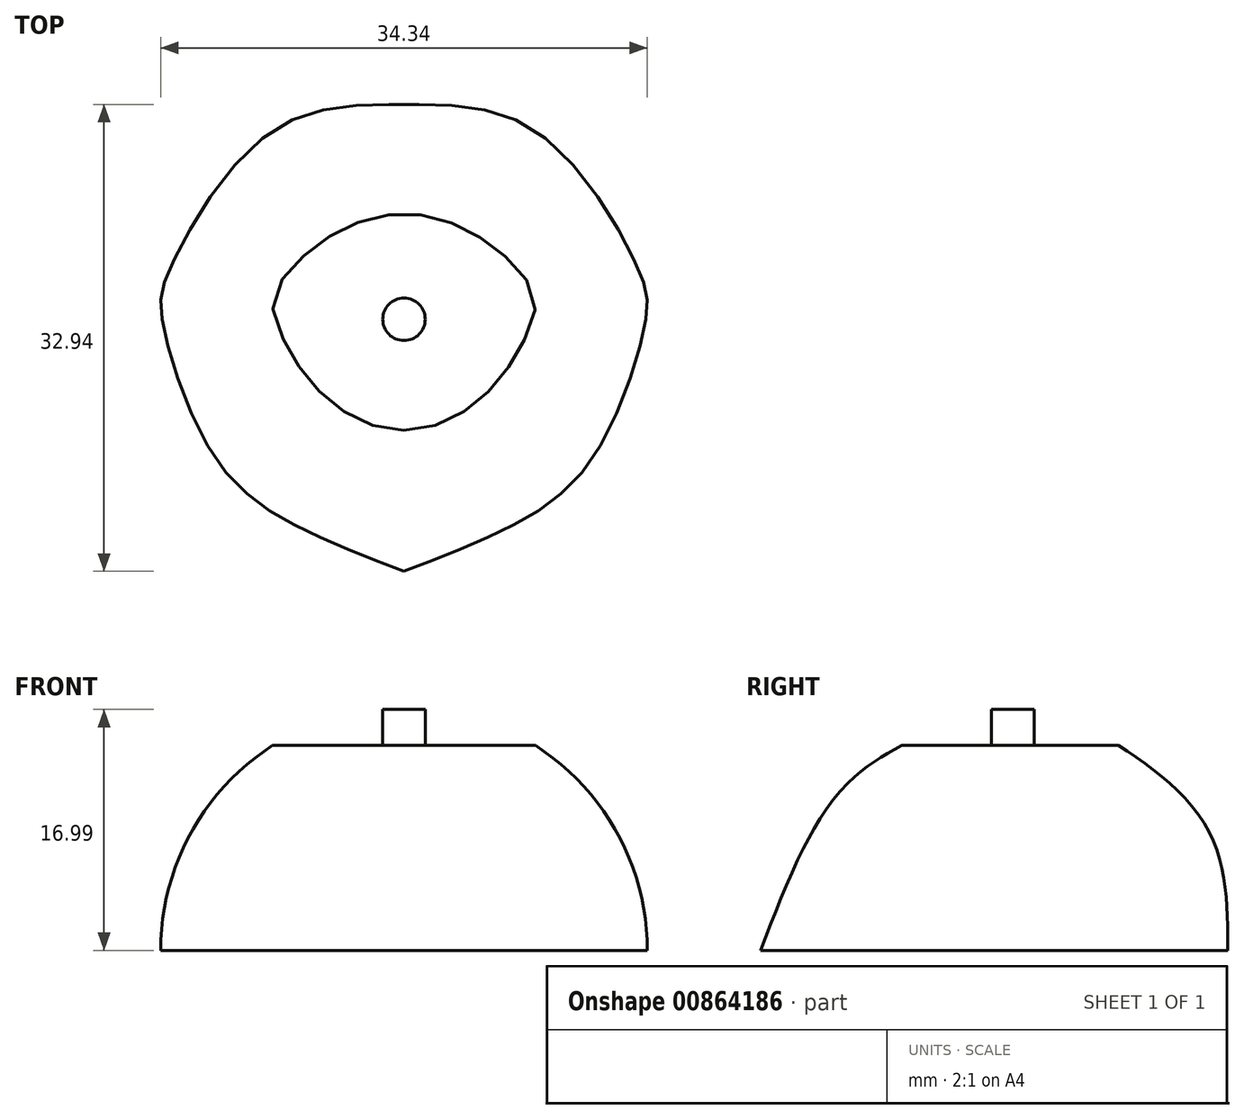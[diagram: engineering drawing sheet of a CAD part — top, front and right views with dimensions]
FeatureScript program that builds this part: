
annotation { "Feature Type Name" : "Feature", "Feature Type Description" : "" }
export const myFeature = defineFeature(function(context is Context, id is Id, definition is map)
    precondition{}
    {
        {
            var Q0;
            Q0=qCreatedBy(makeId("Top.planeOp"),FACE);
            var sketch = newSketch(context, id + "F0", { "sketchPlane" : qUnion([Q0])});
            skLineSegment(sketch, "E0", {"start": v(0, 15.14) * mm, "end": v(0, -17.8) * mm});
            skFitSpline(sketch, "E1", {"points": [v(0, 15.14) * mm, v(-9.57, 13.1) * mm, v(-16.61, 3.33) * mm, v(-17.07, 0) * mm, v(-13.43, -9.62) * mm, v(-7.53, -14.61) * mm, v(0, -17.8) * mm], "startDerivative": vector(-55.12, 0.4) * mm, "endDerivative": vector(47.12, -18.04) * mm});
            skSolve(sketch);
        }
        {
            var Q0;
            Q0=makeQuery(id+"F0.imprint","IMPRINT",FACE,{"disambiguationData":[TD([[makeQuery(id+"F0.imprint","IMPRINT",EDGE,{"derivedFrom":sQuery(id+"F0.wireOp",EDGE,"E0")}),-1.0]])]});
            var Q1;
            Q1=sQuery(id+"F0.wireOp",EDGE,"E0");
            revolve(context, id + "F1", {"surfaceOperationType" : NewSurfaceOperationType.NEW, "entities" : qUnion([Q0]), "axis" : qUnion([Q1]), "revolveType" : RevolveType.FULL});
        }
        {
            var Q0;
            Q0=qCreatedBy(makeId("Front.planeOp"),FACE);
            var sketch = newSketch(context, id + "F2", { "sketchPlane" : qUnion([Q0])});
            skLineSegment(sketch, "E2.bottom", {"start": v(-45.96, 43.21) * mm, "end": v(49.92, 43.21) * mm});
            skLineSegment(sketch, "E2.top", {"start": v(-45.96, 14.45) * mm, "end": v(49.92, 14.45) * mm});
            skLineSegment(sketch, "E2.left", {"start": v(-45.96, 43.21) * mm, "end": v(-45.96, 14.45) * mm});
            skLineSegment(sketch, "E2.right", {"start": v(49.92, 43.21) * mm, "end": v(49.92, 14.45) * mm});
            skLineSegment(sketch, "E3.bottom", {"start": v(-57.56, 0) * mm, "end": v(68.56, 0) * mm});
            skLineSegment(sketch, "E3.top", {"start": v(-57.56, -41.07) * mm, "end": v(68.56, -41.07) * mm});
            skLineSegment(sketch, "E3.left", {"start": v(-57.56, 0) * mm, "end": v(-57.56, -41.07) * mm});
            skLineSegment(sketch, "E3.right", {"start": v(68.56, 0) * mm, "end": v(68.56, -41.07) * mm});
            skSolve(sketch);
        }
        {
            var Q0;
            Q0=makeQuery(id+"F2.imprint","IMPRINT",FACE,{"disambiguationData":[TD([[makeQuery(id+"F2.imprint","IMPRINT",EDGE,{"derivedFrom":sQuery(id+"F2.wireOp",EDGE,"E3.bottom")}),-1.0]])]});
            var Q1;
            Q1=makeQuery(id+"F2.imprint","IMPRINT",FACE,{"disambiguationData":[TD([[makeQuery(id+"F2.imprint","IMPRINT",EDGE,{"derivedFrom":sQuery(id+"F2.wireOp",EDGE,"E2.bottom")}),-1.0]])]});
            extrude(context, id + "F3", {"entities" : qUnion([Q0, Q1]), "operationType" : NewBodyOperationType.REMOVE, "endBound" : BoundingType.SYMMETRIC, "oppositeDirection" : true, "depth" : 50.8 * mm, "offsetDistance" : 25.4 * mm});
        }
        {
            var Q0;
            Q0=makeQuery(id+"F3.boolean.opBoolean","COPY",FACE,{"derivedFrom":makeQuery(id+"F3.opExtrude","SWEPT_FACE",FACE,{"disambiguationData":[OSD([sQuery(id+"F2.wireOp",EDGE,"E2.top")])]})});
            var sketch = newSketch(context, id + "F4", { "sketchPlane" : qUnion([Q0])});
            skCircle(sketch, "E4", {"center": v(0, 0) * mm, "radius": 1.5 * mm});
            skSolve(sketch);
        }
        {
            var Q0;
            Q0=makeQuery(id+"F4.imprint","IMPRINT",FACE,{"disambiguationData":[TD([[makeQuery(id+"F4.imprint","IMPRINT",EDGE,{"derivedFrom":sQuery(id+"F4.wireOp",EDGE,"E4")}),1.0]])]});
            extrude(context, id + "F5", {"entities" : qUnion([Q0]), "operationType" : NewBodyOperationType.ADD, "depth" : 2.54 * mm, "offsetDistance" : 25.4 * mm});
        }
    });
